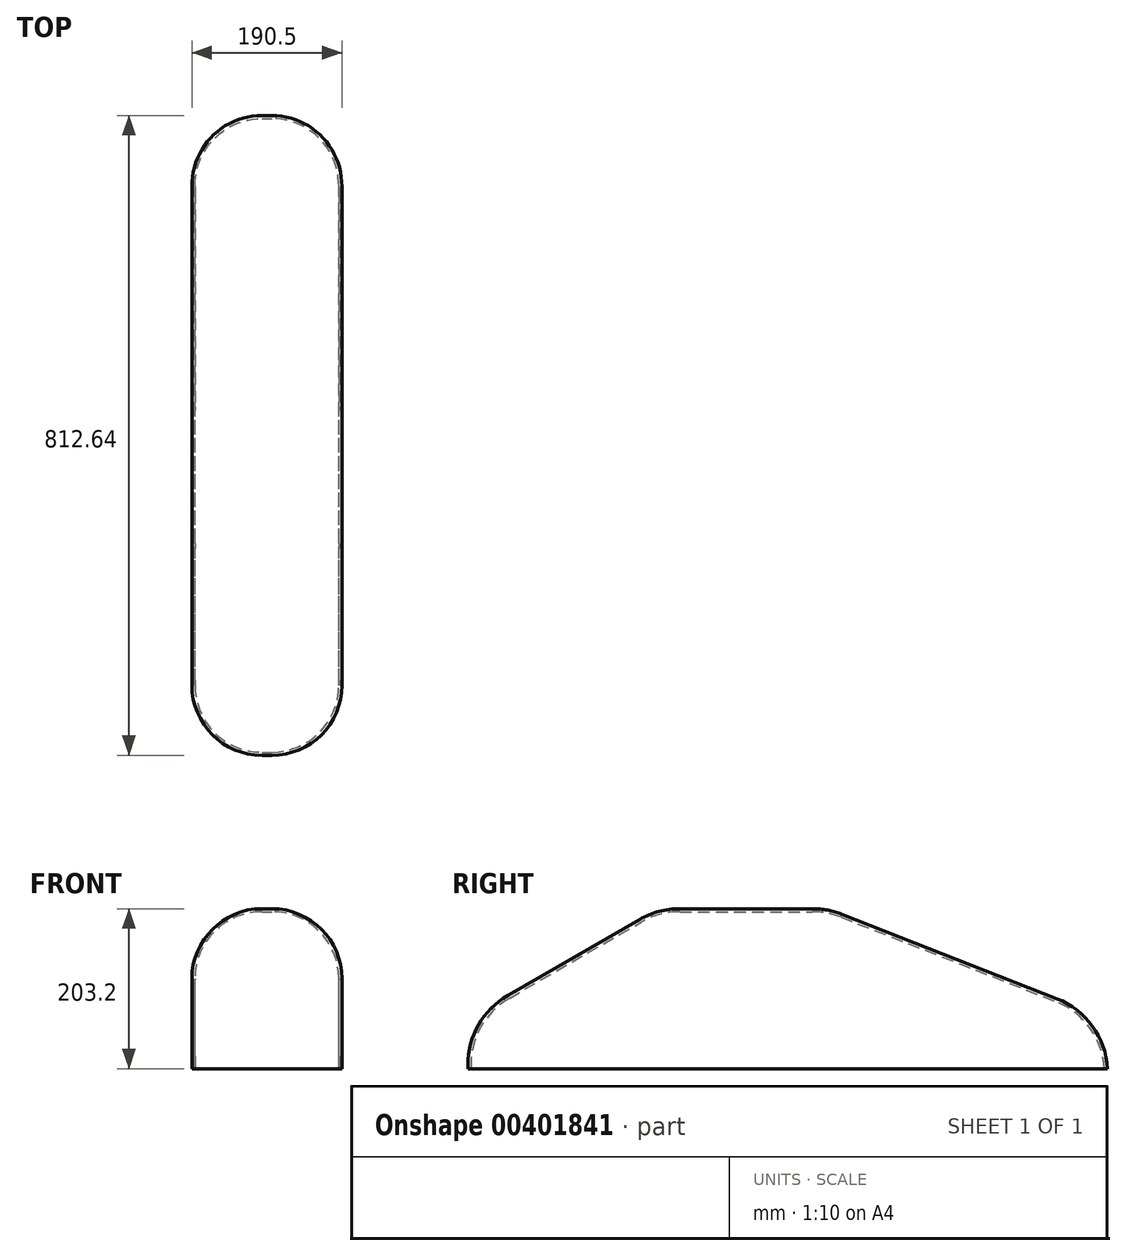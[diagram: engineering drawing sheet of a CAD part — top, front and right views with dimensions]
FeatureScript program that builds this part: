
annotation { "Feature Type Name" : "Feature", "Feature Type Description" : "" }
export const myFeature = defineFeature(function(context is Context, id is Id, definition is map)
    precondition{}
    {
        {
            var Q0;
            Q0=qCreatedBy(makeId("Top.planeOp"),FACE);
            var sketch = newSketch(context, id + "F0", { "sketchPlane" : qUnion([Q0])});
            skLineSegment(sketch, "E0.bottom", {"start": v(95.25, 406.4) * mm, "end": v(-95.25, 406.4) * mm});
            skLineSegment(sketch, "E0.top", {"start": v(95.25, -406.4) * mm, "end": v(-95.25, -406.4) * mm});
            skLineSegment(sketch, "E0.left", {"start": v(95.25, 406.4) * mm, "end": v(95.25, -406.4) * mm});
            skLineSegment(sketch, "E0.right", {"start": v(-95.25, 406.4) * mm, "end": v(-95.25, -406.4) * mm});
            skPoint(sketch, "E0.middle", {"position": v(0, 0) * mm});
            skSolve(sketch);
        }
        {
            var Q0;
            Q0 = qSketchRegion(id + "F0", true);
            extrude(context, id + "F1", {"entities" : qUnion([Q0]), "depth" : 406.4 * mm});
        }
        {
            var Q0;
            Q0=makeQuery(id+"F1.opExtrude","CAP_EDGE",EDGE,{"disambiguationData":[OSD([sQuery(id+"F0.wireOp",EDGE,"E0.top")])],"isStart":false});
            var Q1;
            Q1=makeQuery(id+"F1.opExtrude","CAP_EDGE",EDGE,{"disambiguationData":[OSD([sQuery(id+"F0.wireOp",EDGE,"E0.top")])],"isStart":true});
            chamfer(context, id + "F2", {"entities" : qUnion([Q0, Q1]), "chamferType" : ChamferType.OFFSET_ANGLE, "width" : 139.7 * mm, "oppositeDirection" : false, "angle" : 60 * degree, "tangentPropagation" : true});
        }
        {
            var Q0;
            Q0=makeQuery(id+"F1.opExtrude","CAP_EDGE",EDGE,{"disambiguationData":[OSD([sQuery(id+"F0.wireOp",EDGE,"E0.bottom")])],"isStart":false});
            var Q1;
            Q1=makeQuery(id+"F1.opExtrude","CAP_EDGE",EDGE,{"disambiguationData":[OSD([sQuery(id+"F0.wireOp",EDGE,"E0.bottom")])],"isStart":true});
            chamfer(context, id + "F3", {"entities" : qUnion([Q0, Q1]), "chamferType" : ChamferType.TWO_OFFSETS, "width1" : 355.6 * mm, "oppositeDirection" : false, "width2" : 139.7 * mm, "tangentPropagation" : true});
        }
        {
            var Q0;
            {var subQ0=sQuery(id+"F0.wireOp",EDGE,"E0.top");Q0=makeQuery(id+"F2.opChamfer","BLEND_EDGE",EDGE,{"blendedFrom":[makeQuery(id+"F1.opExtrude","CAP_EDGE",EDGE,{"disambiguationData":[OSD([subQ0])],"isStart":false}),makeQuery(id+"F1.opExtrude","SWEPT_FACE",FACE,{"disambiguationData":[OSD([subQ0])]})],"blendedInto":[makeQuery(id+"F1.opExtrude","SWEPT_FACE",FACE,{"disambiguationData":[OSD([subQ0])]})]});}
            var Q1;
            {var subQ0=sQuery(id+"F0.wireOp",EDGE,"E0.top");Q1=makeQuery(id+"F2.opChamfer","BLEND_EDGE",EDGE,{"blendedFrom":[makeQuery(id+"F1.opExtrude","CAP_EDGE",EDGE,{"disambiguationData":[OSD([subQ0])],"isStart":false}),makeQuery(id+"F1.opExtrude","CAP_FACE",FACE,{"disambiguationData":[OSD([sQuery(id+"F0.wireOp",EDGE,"E0.bottom"),subQ0,sQuery(id+"F0.wireOp",EDGE,"E0.left"),sQuery(id+"F0.wireOp",EDGE,"E0.right")])],"isStart":false})],"blendedInto":[makeQuery(id+"F1.opExtrude","CAP_FACE",FACE,{"disambiguationData":[OSD([sQuery(id+"F0.wireOp",EDGE,"E0.bottom"),subQ0,sQuery(id+"F0.wireOp",EDGE,"E0.left"),sQuery(id+"F0.wireOp",EDGE,"E0.right")])],"isStart":false})]});}
            var Q2;
            {var subQ0=sQuery(id+"F0.wireOp",EDGE,"E0.bottom");Q2=makeQuery(id+"F3.opChamfer","BLEND_EDGE",EDGE,{"blendedFrom":[makeQuery(id+"F1.opExtrude","CAP_EDGE",EDGE,{"disambiguationData":[OSD([subQ0])],"isStart":false}),makeQuery(id+"F1.opExtrude","CAP_FACE",FACE,{"disambiguationData":[OSD([subQ0,sQuery(id+"F0.wireOp",EDGE,"E0.top"),sQuery(id+"F0.wireOp",EDGE,"E0.left"),sQuery(id+"F0.wireOp",EDGE,"E0.right")])],"isStart":false})],"blendedInto":[makeQuery(id+"F1.opExtrude","CAP_FACE",FACE,{"disambiguationData":[OSD([subQ0,sQuery(id+"F0.wireOp",EDGE,"E0.top"),sQuery(id+"F0.wireOp",EDGE,"E0.left"),sQuery(id+"F0.wireOp",EDGE,"E0.right")])],"isStart":false})]});}
            var Q3;
            {var subQ0=sQuery(id+"F0.wireOp",EDGE,"E0.bottom");Q3=makeQuery(id+"F3.opChamfer","BLEND_EDGE",EDGE,{"blendedFrom":[makeQuery(id+"F1.opExtrude","CAP_EDGE",EDGE,{"disambiguationData":[OSD([subQ0])],"isStart":false}),makeQuery(id+"F1.opExtrude","SWEPT_FACE",FACE,{"disambiguationData":[OSD([subQ0])]})],"blendedInto":[makeQuery(id+"F1.opExtrude","SWEPT_FACE",FACE,{"disambiguationData":[OSD([subQ0])]})]});}
            var Q4;
            {var subQ0=sQuery(id+"F0.wireOp",EDGE,"E0.bottom");Q4=makeQuery(id+"F3.opChamfer","BLEND_EDGE",EDGE,{"blendedFrom":[makeQuery(id+"F1.opExtrude","CAP_EDGE",EDGE,{"disambiguationData":[OSD([subQ0])],"isStart":true}),makeQuery(id+"F1.opExtrude","SWEPT_FACE",FACE,{"disambiguationData":[OSD([subQ0])]})],"blendedInto":[makeQuery(id+"F1.opExtrude","SWEPT_FACE",FACE,{"disambiguationData":[OSD([subQ0])]})]});}
            var Q5;
            {var subQ0=sQuery(id+"F0.wireOp",EDGE,"E0.bottom");Q5=makeQuery(id+"F3.opChamfer","BLEND_EDGE",EDGE,{"blendedFrom":[makeQuery(id+"F1.opExtrude","CAP_EDGE",EDGE,{"disambiguationData":[OSD([subQ0])],"isStart":true}),makeQuery(id+"F1.opExtrude","CAP_FACE",FACE,{"disambiguationData":[OSD([subQ0,sQuery(id+"F0.wireOp",EDGE,"E0.top"),sQuery(id+"F0.wireOp",EDGE,"E0.left"),sQuery(id+"F0.wireOp",EDGE,"E0.right")])],"isStart":true})],"blendedInto":[makeQuery(id+"F1.opExtrude","CAP_FACE",FACE,{"disambiguationData":[OSD([subQ0,sQuery(id+"F0.wireOp",EDGE,"E0.top"),sQuery(id+"F0.wireOp",EDGE,"E0.left"),sQuery(id+"F0.wireOp",EDGE,"E0.right")])],"isStart":true})]});}
            var Q6;
            {var subQ0=sQuery(id+"F0.wireOp",EDGE,"E0.top");Q6=makeQuery(id+"F2.opChamfer","BLEND_EDGE",EDGE,{"blendedFrom":[makeQuery(id+"F1.opExtrude","CAP_EDGE",EDGE,{"disambiguationData":[OSD([subQ0])],"isStart":true}),makeQuery(id+"F1.opExtrude","CAP_FACE",FACE,{"disambiguationData":[OSD([sQuery(id+"F0.wireOp",EDGE,"E0.bottom"),subQ0,sQuery(id+"F0.wireOp",EDGE,"E0.left"),sQuery(id+"F0.wireOp",EDGE,"E0.right")])],"isStart":true})],"blendedInto":[makeQuery(id+"F1.opExtrude","CAP_FACE",FACE,{"disambiguationData":[OSD([sQuery(id+"F0.wireOp",EDGE,"E0.bottom"),subQ0,sQuery(id+"F0.wireOp",EDGE,"E0.left"),sQuery(id+"F0.wireOp",EDGE,"E0.right")])],"isStart":true})]});}
            var Q7;
            {var subQ0=sQuery(id+"F0.wireOp",EDGE,"E0.top");Q7=makeQuery(id+"F2.opChamfer","BLEND_EDGE",EDGE,{"blendedFrom":[makeQuery(id+"F1.opExtrude","CAP_EDGE",EDGE,{"disambiguationData":[OSD([subQ0])],"isStart":true}),makeQuery(id+"F1.opExtrude","SWEPT_FACE",FACE,{"disambiguationData":[OSD([subQ0])]})],"blendedInto":[makeQuery(id+"F1.opExtrude","SWEPT_FACE",FACE,{"disambiguationData":[OSD([subQ0])]})]});}
            fillet(context, id + "F4", {"entities" : qUnion([Q0, Q1, Q2, Q3, Q4, Q5, Q6, Q7]), "radius" : 101.6 * mm, "tangentPropagation" : true, "allowEdgeOverflow" : false});
        }
        {
            var Q0;
            Q0=makeQuery(id+"F1.opExtrude","SWEPT_FACE",FACE,{"disambiguationData":[OSD([sQuery(id+"F0.wireOp",EDGE,"E0.left")])]});
            var Q1;
            Q1=makeQuery(id+"F1.opExtrude","SWEPT_FACE",FACE,{"disambiguationData":[OSD([sQuery(id+"F0.wireOp",EDGE,"E0.right")])]});
            fillet(context, id + "F5", {"entities" : qUnion([Q0, Q1]), "radius" : 88.9 * mm, "tangentPropagation" : true, "allowEdgeOverflow" : false});
        }
        {
            var Q0;
            {var subQ0=sQuery(id+"F0.wireOp",EDGE,"E0.left");Q0=makeQuery(id+"F5.opFillet","BLEND_FACE",FACE,{"disambiguationData":[OSD([subQ0]),TDD([makeQuery(id+"F1.opExtrude","CAP_EDGE",EDGE,{"disambiguationData":[OSD([subQ0])],"isStart":true})])]});}
            var Q1;
            Q1=makeQuery(id+"F1.opExtrude","CAP_FACE",FACE,{"disambiguationData":[OSD([sQuery(id+"F0.wireOp",EDGE,"E0.bottom"),sQuery(id+"F0.wireOp",EDGE,"E0.top"),sQuery(id+"F0.wireOp",EDGE,"E0.left"),sQuery(id+"F0.wireOp",EDGE,"E0.right")])],"isStart":true});
            var Q2;
            {var subQ0=sQuery(id+"F0.wireOp",EDGE,"E0.right");Q2=makeQuery(id+"F5.opFillet","BLEND_FACE",FACE,{"disambiguationData":[OSD([subQ0]),TDD([makeQuery(id+"F1.opExtrude","CAP_EDGE",EDGE,{"disambiguationData":[OSD([subQ0])],"isStart":true})])]});}
            shell(context, id + "F6", {"entities" : qUnion([Q0, Q1, Q2]), "thickness" : 3.8 * mm});
        }
        {
            var Q0;
            Q0=makeQuery(id+"F1.opExtrude","SWEPT_FACE",FACE,{"disambiguationData":[OSD([sQuery(id+"F0.wireOp",EDGE,"E0.left")])]});
            var sketch = newSketch(context, id + "F7", { "sketchPlane" : qUnion([Q0])});
            skLineSegment(sketch, "E1.bottom", {"start": v(-563.75, 203.2) * mm, "end": v(419.49, 203.2) * mm});
            skLineSegment(sketch, "E1.top", {"start": v(-563.75, -113.24) * mm, "end": v(419.49, -113.24) * mm});
            skLineSegment(sketch, "E1.left", {"start": v(-563.75, 203.2) * mm, "end": v(-563.75, -113.24) * mm});
            skLineSegment(sketch, "E1.right", {"start": v(419.49, 203.2) * mm, "end": v(419.49, -113.24) * mm});
            skFitSpline(sketch, "E2.0", {"points": [v(316.13, 203.2) * mm, v(346.16, 203.2) * mm, v(376.2, 203.2) * mm, v(406.24, 203.2) * mm]});
            skSolve(sketch);
        }
        {
            var Q0;
            Q0 = qSketchRegion(id + "F7", true);
            extrude(context, id + "F8", {"entities" : qUnion([Q0]), "operationType" : NewBodyOperationType.REMOVE, "endBound" : BoundingType.THROUGH_ALL, "oppositeDirection" : true, "depth" : 25.4 * mm});
        }
    });
